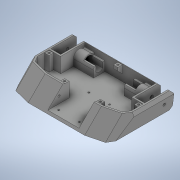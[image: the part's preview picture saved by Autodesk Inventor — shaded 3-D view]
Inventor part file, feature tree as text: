
AUTODESK INVENTOR PART (.ipt)
format: ipt  version: 2020 (Build 240168000, 168)  size: 635,904 bytes
history: native  units: mm
features: extrude x19, sketch x19, projected_geometry x9, chamfer x6, plane x3, mirror x2
ambient origin geometry x8: Origin, YZ Plane, XZ Plane, XY Plane, X Axis, Y Axis, Z Axis, Center Point
bodies: Solid1 (feature_tree)
feature tree (58):
  extrude  "Extrusion1"  Depth=120.0mm
  extrude  "Extrusion2"  TaperAngle=0.0deg  [1 undecoded]
  plane  "Work Plane2"
  extrude  "Extrusion6"  Depth=10.0mm
  plane  "Work Plane4"
  plane  "Work Plane5"
  extrude  "Extrusion7"  TaperAngle=0.0deg  [1 undecoded]
  extrude  "Extrusion8"  Depth=83.204mm TaperAngle=0.0deg
  chamfer  "Chamfer1"  Distance=20.747mm
  chamfer  "Chamfer2"  Distance=27.254mm
  chamfer  "Chamfer3"  Distance=2.0mm Angle=45.0deg
  chamfer  "Chamfer4"  Distance=6.0mm Angle=45.0deg
  chamfer  "Chamfer6"  [1 undecoded]
  extrude  "Extrusion9"  TaperAngle=0.0deg  [1 undecoded]
  extrude  "Extrusion10"  Depth=6.0mm
  extrude  "Extrusion11"  Depth=8.0mm
  extrude  "Extrusion12"  Depth=8.0mm
  mirror  "Mirror2"
  extrude  "WeaponMountSlot"  Depth=8.0mm
  chamfer  "Chamfer7"  Distance=157.438mm
  extrude  "Extrusion14"  Depth=8.0mm
  extrude  "Extrusion15"  Depth=8.0mm TaperAngle=0.0deg
  extrude  "Extrusion16"  Depth=10.0mm TaperAngle=0.0deg
  extrude  "Extrusion17"  Depth=8.0mm
  extrude  "WeaponMountHoles"  Depth=55.8mm
  extrude  "Extrusion19"  Depth=2.0mm TaperAngle=45.0deg
  extrude  "Extrusion20"  Depth=8.0mm
  extrude  "Extrusion21"  Depth=26.0mm
  mirror  "Mirror3"
  extrude  "Extrusion22"  TaperAngle=0.0deg  [1 undecoded]
  sketch  "Sketch1"  dims[d0=180.0mm d1=120.0mm]
  sketch  "Sketch3"  dims[d2=30.0mm d3=0.0mm]
  sketch  "Sketch7"  dims[d4=100.8mm d5=10.0mm]
  projected_geometry  "Projected Loop3"
  sketch  "Sketch9"  dims[d6=10.0mm d7=0.0mm d8=0.0mm]
  sketch  "Sketch10"  dims[d10=45.0deg d18=83.204mm d19=0.0mm d20=20.747mm d21=0.0mm d22=27.254mm d23=0.0mm]
  sketch  "Sketch11"  dims[d24=10.0mm d25=2.0mm d26=45.0deg]
  projected_geometry  "Projected Loop4"
  sketch  "Sketch12"  dims[d27=3.0mm d28=6.0mm d29=45.0deg]
  projected_geometry  "Projected Loop8"
  sketch  "Sketch16"  dims[d30=24.0mm]
  sketch  "Sketch17"  dims[d31=3.0mm]
  sketch  "Sketch18"  dims[d32=45.0deg]
  sketch  "Sketch19"  dims[d33=3.0mm]
  sketch  "Sketch20"  dims[d34=6.0mm]
  projected_geometry  "Projected Loop9"
  projected_geometry  "Projected Loop10"
  projected_geometry  "Projected Loop11"
  projected_geometry  "Projected Loop12"
  sketch  "Sketch21"  dims[d35=45.0deg]
  sketch  "Sketch22"  dims[d39=24.0mm]
  sketch  "Sketch23"  dims[d40=3.0mm]
  sketch  "Sketch24"  dims[d41=45.0deg]
  sketch  "Sketch25"  dims[d45=17.7mm]
  sketch  "Sketch26"  dims[d46=46.15mm d47=0.0mm d48=0.0mm]
  projected_geometry  "Projected Loop13"
  sketch  "Sketch27"  dims[d52=27.0mm d53=0.0mm d58=6.0mm d64=6.5mm d65=16.15mm d66=15.0mm d67=157.438mm d68=0.0mm d69=4.5mm d70=173.156mm d71=0.0mm d72=10.0mm d73=0.0mm d75=37.4mm d76=55.8mm d77=5.0mm d78=2.0mm d79=45.0deg d80=8.0mm d81=26.0mm d82=0.0mm d83=3.75mm d84=3.75mm d85=3.75mm d86=3.75mm d87=7.0mm d88=0.0mm d90=6.0mm d91=4.0mm d92=15.0mm d93=23.0mm d94=7.0mm d95=0.0mm d96=4.0mm d97=15.0mm d98=23.0mm d99=7.0mm d100=0.0mm d101=3.0mm d102=60.0mm d103=3.1mm d104=3.1mm d105=3.1mm d106=3.1mm d107=10.0mm d108=9.4mm d109=9.4mm d110=64.0mm d111=64.0mm d112=9.4mm d113=9.4mm d114=10.0mm d115=27.0mm d116=0.0mm d117=6.1mm d118=0.0mm d119=-7.853982mm d120=16.3mm d121=16.15mm d122=15.0mm d123=2.0mm d124=20.3mm d125=17.0mm d126=0.0mm d127=15.5mm d128=12.2mm d129=19.0mm d130=0.0mm d131=45.0deg d133=19.0mm d134=0.0mm d135=8.0mm d137=6.1mm]
  projected_geometry  "Projected Loop14"
note: 5 required parameter values undecoded (feature->parameter linkage not recoverable at this tier; creation-order binding heuristic only, values carry confidence <= 0.55)
